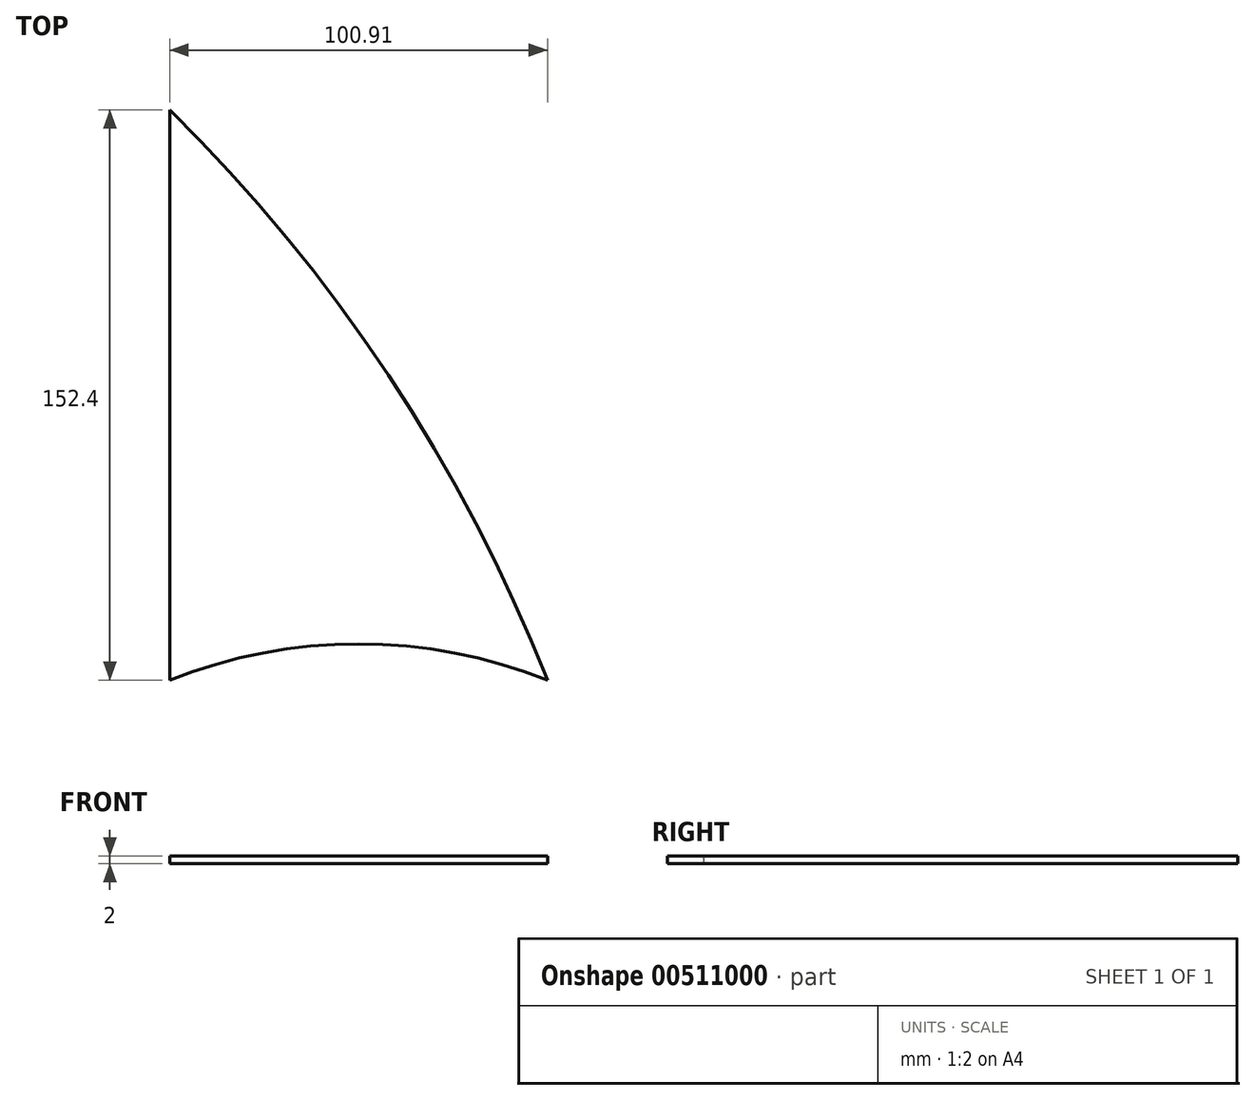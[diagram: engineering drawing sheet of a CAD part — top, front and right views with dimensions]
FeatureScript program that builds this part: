
annotation { "Feature Type Name" : "Feature", "Feature Type Description" : "" }
export const myFeature = defineFeature(function(context is Context, id is Id, definition is map)
    precondition{}
    {
        {
            var Q0;
            Q0=qCreatedBy(makeId("Top.planeOp"),FACE);
            var sketch = newSketch(context, id + "F0", { "sketchPlane" : qUnion([Q0])});
            skLineSegment(sketch, "E0", {"start": v(-69.24, 80.01) * mm, "end": v(-69.24, -72.39) * mm});
            skArc(sketch, "E1", {"start": v(31.67, -72.39) * mm, "mid": v(-18.78, -62.7) * mm, "end": v(-69.24, -72.39) * mm});
            skArc(sketch, "E2", {"start": v(31.67, -72.39) * mm, "mid": v(-10.8, 9.1) * mm, "end": v(-69.24, 80.01) * mm});
            skSolve(sketch);
        }
        {
            var Q0;
            Q0=makeQuery(id+"F0.imprint","IMPRINT",FACE,{"disambiguationData":[TD([[makeQuery(id+"F0.imprint","IMPRINT",EDGE,{"derivedFrom":sQuery(id+"F0.wireOp",EDGE,"E0")}),1.0]])]});
            extrude(context, id + "F1", {"entities" : qUnion([Q0]), "depth" : 2 * mm, "offsetDistance" : 25 * mm});
        }
    });
